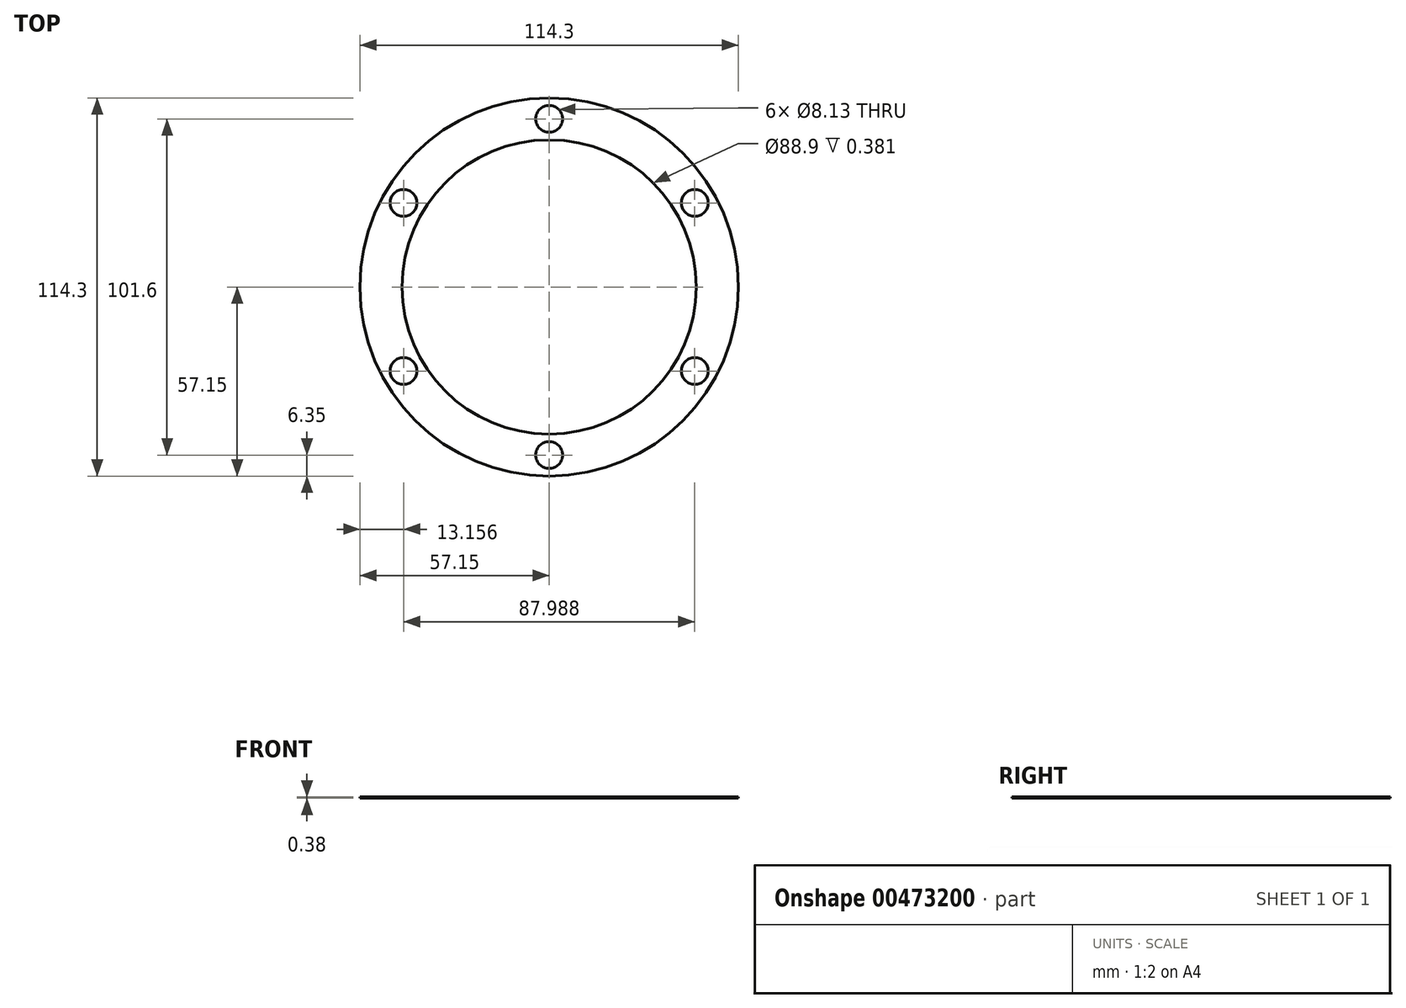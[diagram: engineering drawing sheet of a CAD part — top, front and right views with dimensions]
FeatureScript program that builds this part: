
annotation { "Feature Type Name" : "Feature", "Feature Type Description" : "" }
export const myFeature = defineFeature(function(context is Context, id is Id, definition is map)
    precondition{}
    {
        {
            var Q0;
            Q0=qCreatedBy(makeId("Top.planeOp"),FACE);
            var sketch = newSketch(context, id + "F0", { "sketchPlane" : qUnion([Q0])});
            skCircle(sketch, "E0", {"center": v(0, 0) * mm, "radius": 57.15 * mm});
            skCircle(sketch, "E1", {"center": v(0, 0) * mm, "radius": 44.45 * mm});
            skCircle(sketch, "E2", {"center": v(0, 0) * mm, "radius": 50.8 * mm, "construction": true});
            skCircle(sketch, "E3", {"center": v(0, 50.8) * mm, "radius": 4.06 * mm});
            skCircle(sketch, "E4.1.0", {"center": v(44, 25.4) * mm, "radius": 4.06 * mm});
            skCircle(sketch, "E4.2.0", {"center": v(44, -25.4) * mm, "radius": 4.06 * mm});
            skLineSegment(sketch, "E4.anchor1", {"start": v(0, 0) * mm, "end": v(0, 50.8) * mm, "construction": true});
            skLineSegment(sketch, "E4.anchor2", {"start": v(0, 0) * mm, "end": v(44, -25.4) * mm, "construction": true});
            skCircle(sketch, "E5.1.0", {"center": v(-44, -25.4) * mm, "radius": 4.06 * mm});
            skCircle(sketch, "E5.1.1", {"center": v(-44, 25.4) * mm, "radius": 4.06 * mm});
            skCircle(sketch, "E5.2.1", {"center": v(0, -50.8) * mm, "radius": 4.06 * mm});
            skCircle(sketch, "E5.2.2", {"center": v(-44, -25.4) * mm, "radius": 4.06 * mm});
            skSolve(sketch);
        }
        {
            var Q0;
            Q0 = qSketchRegion(id + "F0", true);
            extrude(context, id + "F1", {"entities" : qUnion([Q0]), "depth" : 0.38 * mm});
        }
    });
